# Revit family: TemID_Контрольный считыватель для карт и меток_UHF RFID UR20RW-E
name_source: partatom
category: Обобщенные модели
units: mm (PartAtom-declared; Revit-internal decimal feet)

## family parameters
Всегда вертикально = Нет
Может служить основой для арматурных стержней = Нет
На основе рабочей плоскости = Нет
Общий = Нет
При загрузке вырезать с полостями = Нет
Размер круглого соединителя = Использовать диаметр
Тип детали = Нормальный
Точка расчета площади = Да

## types (1)
- UHF RFID UR20RW-E
    =Габариты= = =Габариты=
    ADSK_Группирование = 3. Периферийное оборудование
    ADSK_Единица измерения = шт.
    ADSK_Количество = 1
    ADSK_Марка = UHF RFID UR20RW-E
    ADSK_Наименование = Контрольный считыватель для карт и меток
    ADSK_Размер_Высота = 107 мм
    ADSK_Размер_Глубина = 23 мм
    ADSK_Размер_Ширина = 107 мм
    ADSK_Тип = UHF RFID UR20RW-E
    Зона обслуживания_Отступ от прибора = 100 мм
    Материал = Белый
    Отметка по умолчанию = 0 мм
    Текст модели = UR20RW-E
    Тип геометрии = ВЛ_НО_СС_Геометрия_поворотного_семейства : ASML_ВЛ_НО_СС_Геометрия_поворотного_семейства
    УГО_Тип = ASML_УГО_СКУД_Считыватель : ASML_УГО_СКУД_Считыватель_внутренний
